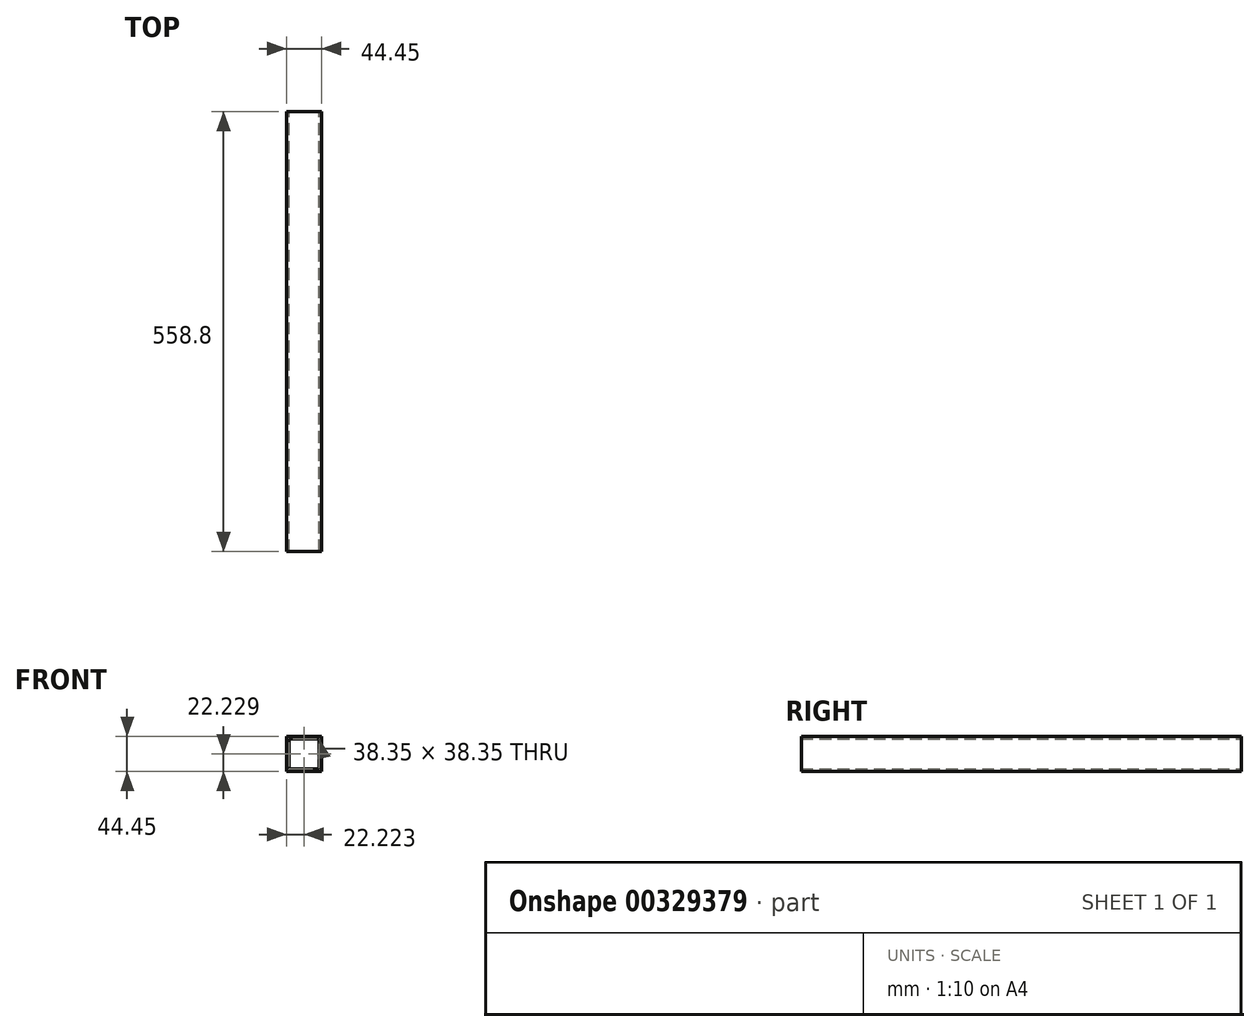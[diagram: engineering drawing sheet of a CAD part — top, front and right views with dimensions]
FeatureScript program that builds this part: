
annotation { "Feature Type Name" : "Feature", "Feature Type Description" : "" }
export const myFeature = defineFeature(function(context is Context, id is Id, definition is map)
    precondition{}
    {
        {
            var Q0;
            Q0=qCreatedBy(makeId("Front.planeOp"),FACE);
            var sketch = newSketch(context, id + "F0", { "sketchPlane" : qUnion([Q0])});
            skLineSegment(sketch, "E0", {"start": v(-22.61, 34.34) * mm, "end": v(21.84, 34.34) * mm});
            skLineSegment(sketch, "E1", {"start": v(21.84, 34.34) * mm, "end": v(21.84, -10.1) * mm});
            skLineSegment(sketch, "E2", {"start": v(21.84, -10.1) * mm, "end": v(-22.61, -10.1) * mm});
            skLineSegment(sketch, "E3", {"start": v(-22.61, -10.1) * mm, "end": v(-22.61, 34.34) * mm});
            skLineSegment(sketch, "E4.0", {"start": v(-19.56, 31.3) * mm, "end": v(18.79, 31.3) * mm});
            skLineSegment(sketch, "E4.1", {"start": v(-19.56, -7.06) * mm, "end": v(-19.56, 31.3) * mm});
            skLineSegment(sketch, "E4.2", {"start": v(18.79, -7.06) * mm, "end": v(-19.56, -7.06) * mm});
            skLineSegment(sketch, "E4.3", {"start": v(18.79, 31.3) * mm, "end": v(18.79, -7.06) * mm});
            skSolve(sketch);
        }
        {
            var Q0;
            Q0=makeQuery(id+"F0.imprint","IMPRINT",FACE,{"disambiguationData":[TD([[makeQuery(id+"F0.imprint","IMPRINT",EDGE,{"derivedFrom":sQuery(id+"F0.wireOp",EDGE,"E0")}),-1.0]])]});
            var Q1;
            Q1=sQuery(id+"F0.wireOp",EDGE,"E1");
            var Q2;
            Q2=sQuery(id+"F0.wireOp",EDGE,"E2");
            var Q3;
            Q3=sQuery(id+"F0.wireOp",EDGE,"E4.2");
            var Q4;
            Q4=sQuery(id+"F0.wireOp",EDGE,"E4.3");
            var Q5;
            Q5=sQuery(id+"F0.wireOp",EDGE,"E4.1");
            var Q6;
            Q6=sQuery(id+"F0.wireOp",EDGE,"E4.0");
            var Q7;
            Q7=sQuery(id+"F0.wireOp",EDGE,"E0");
            var Q8;
            Q8=sQuery(id+"F0.wireOp",EDGE,"E3");
            extrude(context, id + "F1", {"entities" : qUnion([Q0]), "surfaceEntities" : qUnion([Q1, Q2, Q3, Q4, Q5, Q6, Q7, Q8]), "depth" : 558.8 * mm});
        }
    });
